# Revit family: OWDRL
name_source: partatom
category: Mechanical Equipment
units: mm (PartAtom-declared; Revit-internal decimal feet)

## family parameters
Always vertical = Yes
Cut with Voids When Loaded = No
OmniClass Number = 23.40.40.11.17
OmniClass Title = Refrigerated Cases
Part Type = Normal
Room Calculation Point = No
Round Connector Dimension = Use Radius
Shared = No
Work Plane-Based = Yes

## types (2) — shared parameters
10" Shelf = Yes
8" Shelf = Yes
ANTI CON AMPS = 0 A
BOTTOM ELECTRICAL = Yes
BOTTOM REFRIGERATION PIPING = Yes
Certifications = NSF 7, UL471, CSA
DATE = 05/19/2017
DEFROST AMPS = 0 A
DISCHARGE AIR TEMP = 0 °F
DISCHARGE AIR VELOCITY = -(FPM)
DRAIN HEATERS AMPS = 0 A
DRAIN LINE CONNECTION = SANITARY CONNECTION
DRAIN LINE DIAMETER = 2"
DRAIN PIPE TYPE = PVC
DRAIN PIPING = Yes
DRIP PAN PLUMB TYPE = HARD
Default Elevation = 48"
Defrost Termination = - °F
Defrost Type = TIMED-OFF DEFROST
Description = Roll-In Front Load Merchandiser
END PANEL = <By Category>
EQUIPMENT DESCRIPTION = Roll-In Front Load Merchandiser
EQUIPMENT MARK = OWDRL
Ends = Yes
GLASS = Glass
HIGH EFFICIENCY FANS AMPS = 0 A
Height = 81 3/4"
Item Description = Roll-In Front Load Merchandiser
LF STD END = Yes
LIGHT AMPS = 0 A
LIQUID LINE CONNECTION = LIQUID LINE CONNECTION
LIQUID LINE DIAMETER = 0"
LIQUID LINE RADIUS = 0"
LOAD 1 CLASSIFICATION = Lighting
LOAD 1 DESCRIPTION = LIGHTS - STANDARD POWER (SHELF or CORNICE)
LOAD 1 PLUG TYPE = HARDWIRED
LOAD 1 POLES = 1
LOAD 1 VOLTAGE = 120 V
LOAD 1 WATTAGE = 0 W
LOAD 2 CLASSIFICATION = Motor
LOAD 2 DESCRIPTION = HIGH EFFICIENCY FANS CONNECTION
LOAD 2 PLUG TYPE = HARDWIRED
LOAD 2 POLES = 1
LOAD 2 VOLTAGE = 120 V
LOAD 2 WATTAGE = 0 W
LOAD 3 CLASSIFICATION = Power
LOAD 3 DESCRIPTION = ANTI-SWEAT CONNECTION
LOAD 3 PLUG TYPE = HARDWIRED
LOAD 3 POLES = 1
LOAD 3 VOLTAGE = 120 V
LOAD 3 WATTAGE = 0 W
LOAD 4 DESCRIPTION = DEFROST HEATER CONNECTION
LOAD 4 PLUG TYPE = HARDWIRED
LOAD 4 POLES = 1
LOAD 4 VOLTAGE = 208 V
LOAD 4 WATTAGE = 0 W
LOAD 5 DESCRIPTION = DRAIN HEATER CONNECTION
LOAD 5 PLUG TYPE = HARDWIRED
LOAD 5 POLES = 1
LOAD 5 VOLTAGE = 120 V
LOAD 5 WATTAGE = 0 W
Legend Number = OWDRL
Manufacturer = HILL PHOENIX
Model = OWDRL
Number of Shelf = 3
PAINTED METAL UPPER SHELF = PAINTED SHELVES
PRESSURE REGULATOR = 0.00 psi
REAR REFRIGERATION PIPING = Yes
REFRIGERATION PIPING = COPPER PIPE
RT STD END = Yes
Ref Plane = 28 5/8"
Refgn = 8 5/8"
Refrig Charge Lbs = -
SANITARY PIPE SIZE = 1"
STAINLESS STEEL = GALVANIZED STEEL
SUCTION LINE CONNECTION = SUCTION LINE CONNECTION
SUCTION LINE DIAMETER = 1"
SUCTION LINE RADIUS = 0"
Shelf distance = 48"
TOP ELECTRICAL = Yes
TOP REFRIGERATION PIPING = Yes
URL = http://www.hillphoenix.com
Width = 67 1/2"
zero-valued in all types: Defrost Num Day, Evap Temp, Load Mbh, POWER FACTOR

## per-type parameters (varying)
| type | CENTER LINE | Door | Length | Number of Doors |
| OWDRL-8' | 48" | Door 8' : OGM-8' | 96" | 2 |
| OWDRL-12' | 72" | Door 12' : OGM-12' | 144" | 3 |

## geometry (parser evidence)
native form markers: Blend x13, Sweep x11
no freeform markers — native parametric forms only
